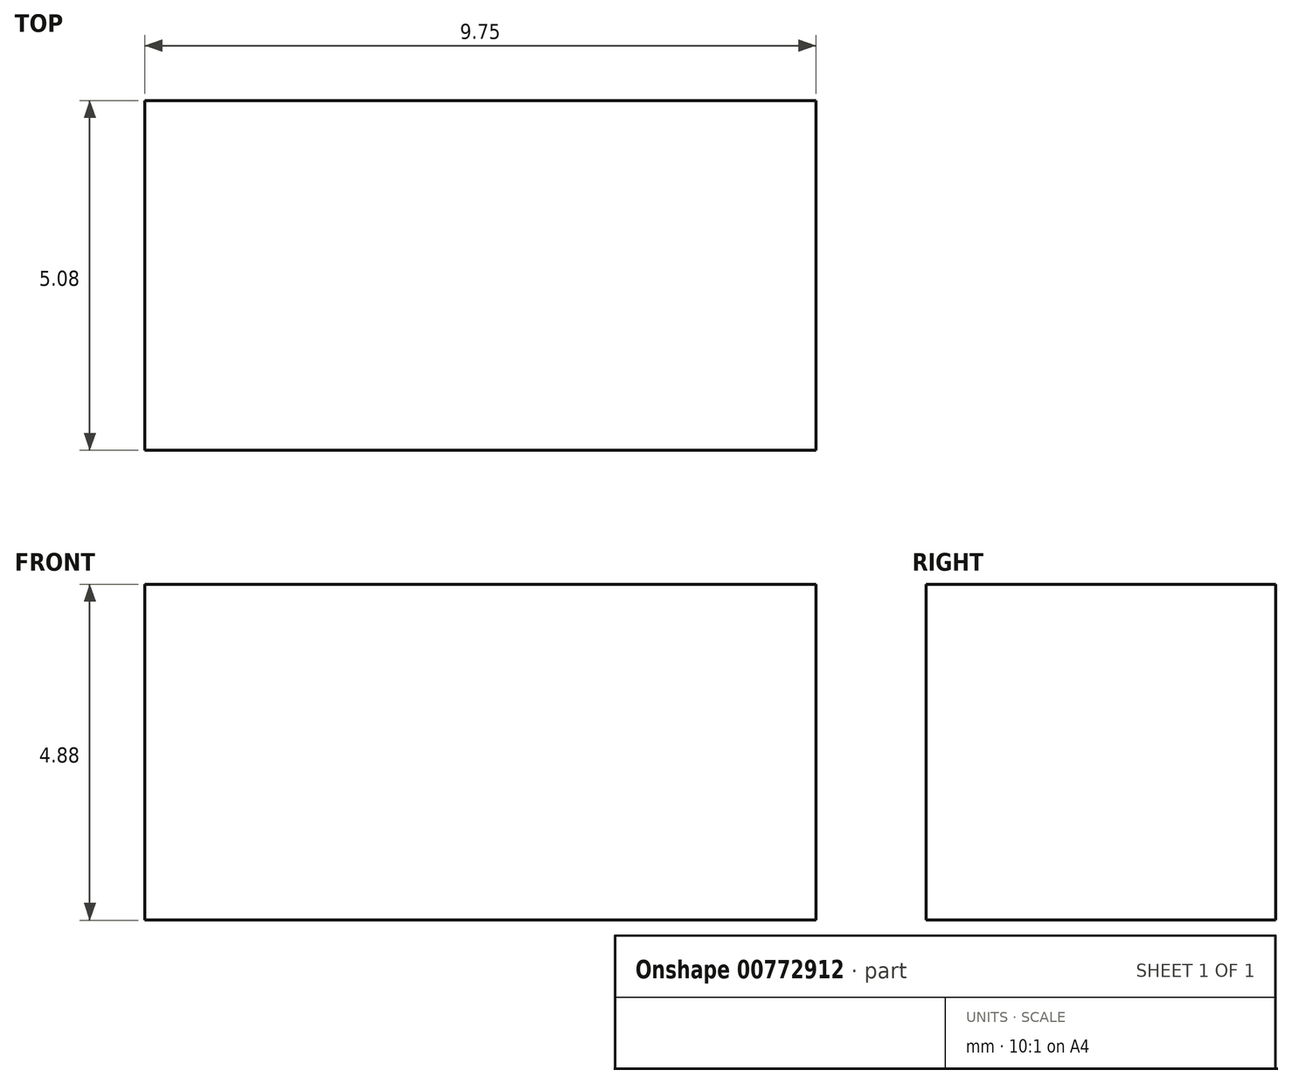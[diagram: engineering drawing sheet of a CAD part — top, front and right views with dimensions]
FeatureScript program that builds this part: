
annotation { "Feature Type Name" : "Feature", "Feature Type Description" : "" }
export const myFeature = defineFeature(function(context is Context, id is Id, definition is map)
    precondition{}
    {
        {
            var Q0;
            Q0=qCreatedBy(makeId("Front.planeOp"),FACE);
            var sketch = newSketch(context, id + "F0", { "sketchPlane" : qUnion([Q0])});
            skLineSegment(sketch, "E0.bottom", {"start": v(-46.48, 19.2) * mm, "end": v(-36.73, 19.2) * mm});
            skLineSegment(sketch, "E0.top", {"start": v(-46.48, 24.08) * mm, "end": v(-36.73, 24.08) * mm});
            skLineSegment(sketch, "E0.left", {"start": v(-46.48, 19.2) * mm, "end": v(-46.48, 24.08) * mm});
            skLineSegment(sketch, "E0.right", {"start": v(-36.73, 19.2) * mm, "end": v(-36.73, 24.08) * mm});
            skPoint(sketch, "E0.middle", {"position": v(-41.6, 21.64) * mm});
            skSolve(sketch);
        }
        {
            var Q0;
            Q0 = qSketchRegion(id + "F0", true);
            extrude(context, id + "F1", {"entities" : qUnion([Q0]), "depth" : 5.08 * mm, "offsetDistance" : 25.4 * mm});
        }
    });
